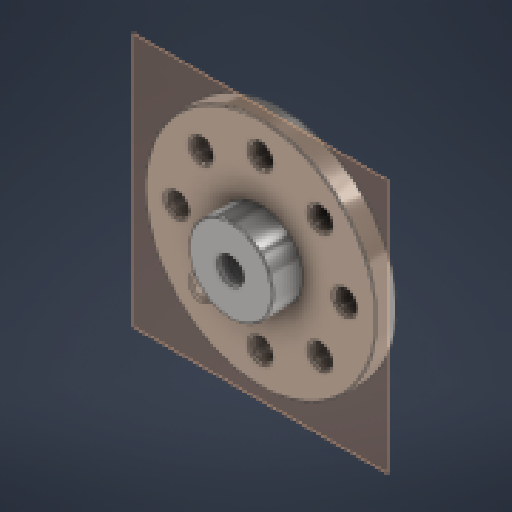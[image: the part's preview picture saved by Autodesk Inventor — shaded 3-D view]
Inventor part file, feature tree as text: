
AUTODESK INVENTOR PART (.ipt)
format: ipt  version: 2024 (Build 280153000, 153)  size: 205,824 bytes
history: native  units: mm
features: other x7, sketch x2, extrude x2, reference x2, fillet x1, chamfer x1, projected_geometry x1
ambient origin geometry x8: Origin, YZ Plane, XZ Plane, XY Plane, X Axis, Y Axis, Z Axis, Center Point
bodies: Body1 (feature_tree)
feature tree (16):
  other  "솔리드1"
  other  "작업 평면1"
  sketch  "스케치1"
  other  "작업 평면2"
  extrude  "돌출1"  Depth=2.5mm
  sketch  "스케치2"
  other  "작업 평면3"
  extrude  "돌출2"  Depth=10.0mm TaperAngle=0.0deg
  fillet  "모깎기1"  Radius=10.0mm
  other  "스레드1"
  chamfer  "모따기1"  Distance=0.1mm
  reference  "참조1"
  reference  "참조2"
  projected_geometry  "투영된 루프1"
  other  "MX-28T_R+idle.ipt.iam"
  other  "MX-28T_R:1"
